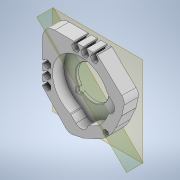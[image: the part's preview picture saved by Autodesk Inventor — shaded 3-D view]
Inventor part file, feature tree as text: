
AUTODESK INVENTOR PART (.ipt)
format: ipt  version: 2022 (Build 260153000, 153)  size: 740,864 bytes
history: native  units: in
note: dims shown in document units (in); Inventor stores cm internally (conversion verified against a paired STEP export)
features: reference x8, extrude x3, fillet x3, sketch x3, other x3, plane x2, chamfer x1, projected_geometry x1
ambient origin geometry x8: Origin, YZ Plane, XZ Plane, XY Plane, X Axis, Y Axis, Z Axis, Center Point
bodies: Solid1 (feature_tree)
feature tree (24):
  plane  "Work Plane1"
  extrude  "Extrusion1"  Depth=1.0in
  extrude  "Extrusion2"  Depth=0.1575in
  plane  "Work Plane2"
  fillet  "Fillet3"  Radius=0.7874in
  fillet  "Fillet4"  Radius=0.1575in
  chamfer  "Chamfer3"  Distance=1.0in
  extrude  "Extrusion3"  TaperAngle=315.0deg  [1 undecoded]
  fillet  "Fillet2"  Radius=0.75in
  sketch  "Sketch1"  dims[d0=1.75in d1=1.0in]
  reference  "Reference1"
  sketch  "Sketch2"  dims[d2=45.0deg d3=0.1679in d4=0.7874in d6=360.0deg d8=0.1575in d9=0.0in]
  projected_geometry  "Projected Loop1"
  sketch  "Sketch3"  dims[d10=1.0in d11=1.0in d12=315.0deg d13=0.75in d14=135.0deg d15=0.6in d16=0.0in d18=45.0deg d19=0.0in d20=0.0in d21=0.125in d23=3.0in d24=0.261in d25=0.0394in d26=0.125in d33=0.0236in d34=0.125in d35=45.0deg]
  reference  "Reference2"
  reference  "Reference3"
  reference  "Reference4"
  reference  "Reference5"
  reference  "Reference6"
  reference  "Reference7"
  reference  "Reference8"
  other  "<userpath>\Documents\CAD\guardSwerve1\Assembly1.iam"
  other  "Assembly1.iam"
  other  "midblock"
note: 1 required parameter value undecoded (feature->parameter linkage not recoverable at this tier; creation-order binding heuristic only, values carry confidence <= 0.55)
